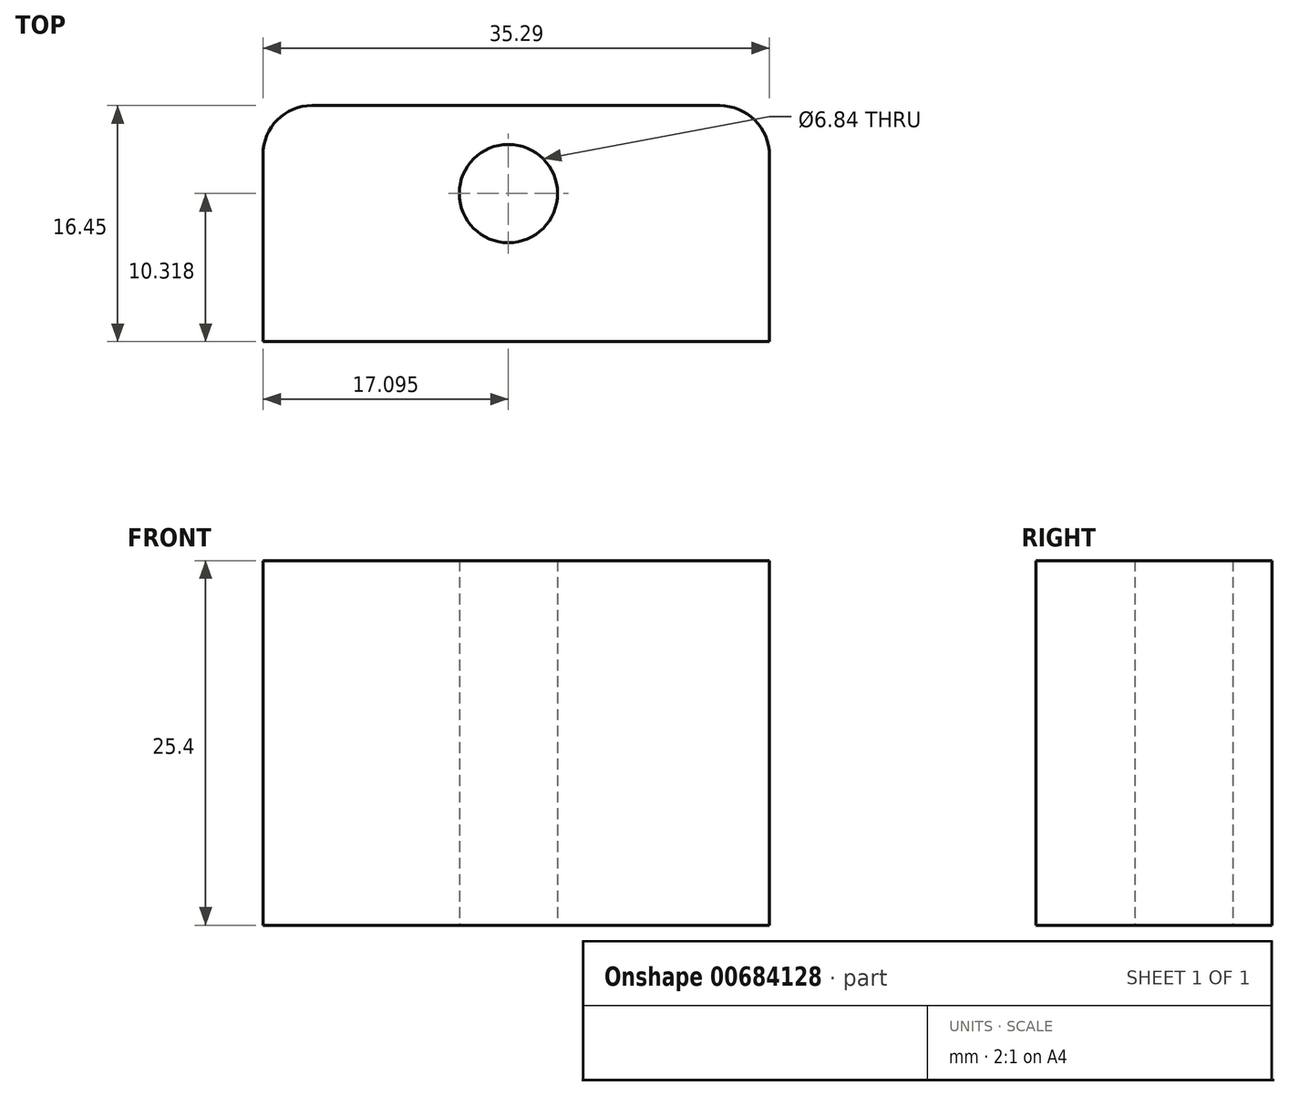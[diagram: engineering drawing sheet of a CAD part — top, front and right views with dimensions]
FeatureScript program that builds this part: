
annotation { "Feature Type Name" : "Feature", "Feature Type Description" : "" }
export const myFeature = defineFeature(function(context is Context, id is Id, definition is map)
    precondition{}
    {
        {
            var Q0;
            Q0=qCreatedBy(makeId("Top.planeOp"),FACE);
            var sketch = newSketch(context, id + "F0", { "sketchPlane" : qUnion([Q0])});
            skLineSegment(sketch, "E0.bottom", {"start": v(-9.54, 7.39) * mm, "end": v(18.86, 7.39) * mm});
            skLineSegment(sketch, "E0.top", {"start": v(-12.95, -9.06) * mm, "end": v(22.34, -9.06) * mm});
            skLineSegment(sketch, "E0.left", {"start": v(-12.95, 3.98) * mm, "end": v(-12.95, -9.06) * mm});
            skLineSegment(sketch, "E0.right", {"start": v(22.34, 3.9) * mm, "end": v(22.34, -9.06) * mm});
            skPoint(sketch, "E1.visualSharp", {"position": v(-12.95, 7.39) * mm});
            skArc(sketch, "E1.filletArc", {"start": v(-9.54, 7.39) * mm, "mid": v(-11.95, 6.39) * mm, "end": v(-12.95, 3.98) * mm});
            skPoint(sketch, "E2.visualSharp", {"position": v(22.34, 7.39) * mm});
            skArc(sketch, "E2.filletArc", {"start": v(22.34, 3.9) * mm, "mid": v(21.32, 6.37) * mm, "end": v(18.86, 7.39) * mm});
            skCircle(sketch, "E3", {"center": v(4.14, 1.26) * mm, "radius": 3.42 * mm});
            skSolve(sketch);
        }
        {
            var Q0;
            Q0 = qSketchRegion(id + "F0", true);
            extrude(context, id + "F1", {"entities" : qUnion([Q0]), "depth" : 25.4 * mm, "offsetDistance" : 25.4 * mm});
        }
    });
